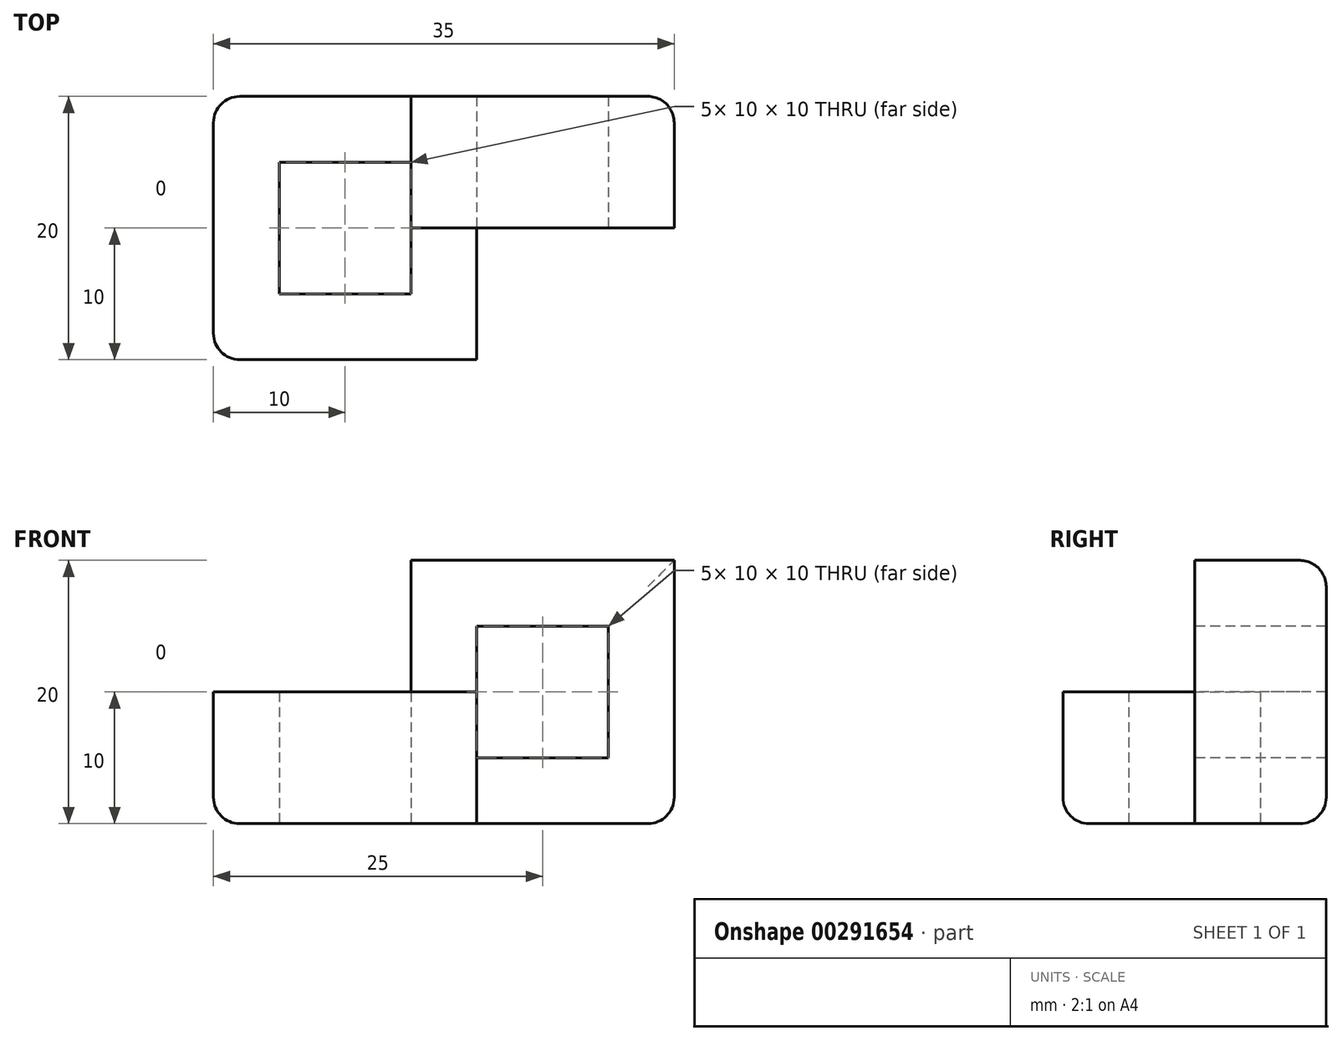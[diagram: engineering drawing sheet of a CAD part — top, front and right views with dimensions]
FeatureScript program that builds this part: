
annotation { "Feature Type Name" : "Feature", "Feature Type Description" : "" }
export const myFeature = defineFeature(function(context is Context, id is Id, definition is map)
    precondition{}
    {
        {
            var Q0;
            Q0=qCreatedBy(makeId("Top.planeOp"),FACE);
            var sketch = newSketch(context, id + "F0", { "sketchPlane" : qUnion([Q0])});
            skLineSegment(sketch, "E0.bottom", {"start": v(0, 0) * mm, "end": v(10, 0) * mm});
            skLineSegment(sketch, "E0.top", {"start": v(0, 10) * mm, "end": v(10, 10) * mm});
            skLineSegment(sketch, "E0.left", {"start": v(0, 0) * mm, "end": v(0, 10) * mm});
            skLineSegment(sketch, "E0.right", {"start": v(10, 0) * mm, "end": v(10, 10) * mm});
            skLineSegment(sketch, "E1.bottom", {"start": v(-5, 15) * mm, "end": v(30, 15) * mm});
            skLineSegment(sketch, "E1.top", {"start": v(-5, -5) * mm, "end": v(30, -5) * mm});
            skLineSegment(sketch, "E1.left", {"start": v(-5, 15) * mm, "end": v(-5, -5) * mm});
            skLineSegment(sketch, "E1.right", {"start": v(30, 15) * mm, "end": v(30, -5) * mm});
            skSolve(sketch);
        }
        {
            var Q0;
            Q0=makeQuery(id+"F0.imprint","IMPRINT",FACE,{"disambiguationData":[TD([[makeQuery(id+"F0.imprint","IMPRINT",EDGE,{"derivedFrom":sQuery(id+"F0.wireOp",EDGE,"E0.bottom")}),-1.0]])]});
            extrude(context, id + "F1", {"entities" : qUnion([Q0]), "depth" : 20 * mm});
        }
        {
            var Q0;
            Q0=makeQuery(id+"F1.opExtrude","SWEPT_FACE",FACE,{"disambiguationData":[OSD([sQuery(id+"F0.wireOp",EDGE,"E1.top")])]});
            var sketch = newSketch(context, id + "F2", { "sketchPlane" : qUnion([Q0])});
            skLineSegment(sketch, "E2.bottom", {"start": v(15, 15) * mm, "end": v(25, 15) * mm});
            skLineSegment(sketch, "E2.top", {"start": v(15, 5) * mm, "end": v(25, 5) * mm});
            skLineSegment(sketch, "E2.left", {"start": v(15, 15) * mm, "end": v(15, 5) * mm});
            skLineSegment(sketch, "E2.right", {"start": v(25, 15) * mm, "end": v(25, 5) * mm});
            skLineSegment(sketch, "E3", {"start": v(10, 20) * mm, "end": v(10, 0) * mm});
            skLineSegment(sketch, "E4", {"start": v(-5, 10) * mm, "end": v(30, 10) * mm});
            skLineSegment(sketch, "E5", {"start": v(15, 5) * mm, "end": v(15, 0) * mm});
            skSolve(sketch);
        }
        {
            var Q0;
            Q0=makeQuery(id+"F2.imprint","IMPRINT",FACE,{"disambiguationData":[TD([[makeQuery(id+"F2.imprint","IMPRINT",EDGE,{"derivedFrom":sQuery(id+"F2.wireOp",EDGE,"E2.bottom")}),-1.0]])]});
            var Q1;
            {var subQ0=sQuery(id+"F2.wireOp",EDGE,"E2.top");Q1=makeQuery(id+"F2.imprint","IMPRINT",FACE,{"disambiguationData":[TD([[makeQuery(id+"F2.imprint","IMPRINT",EDGE,{"derivedFrom":subQ0}),1.0]])]});}
            extrude(context, id + "F3", {"entities" : qUnion([Q0, Q1]), "operationType" : NewBodyOperationType.REMOVE, "oppositeDirection" : true, "depth" : 25 * mm});
        }
        {
            var Q0;
            Q0=makeQuery(id+"F1.opExtrude","CAP_FACE",FACE,{"disambiguationData":[OSD([sQuery(id+"F0.wireOp",EDGE,"E0.bottom"),sQuery(id+"F0.wireOp",EDGE,"E0.top"),sQuery(id+"F0.wireOp",EDGE,"E0.left"),sQuery(id+"F0.wireOp",EDGE,"E0.right"),sQuery(id+"F0.wireOp",EDGE,"E1.bottom"),sQuery(id+"F0.wireOp",EDGE,"E1.top"),sQuery(id+"F0.wireOp",EDGE,"E1.left"),sQuery(id+"F0.wireOp",EDGE,"E1.right")])],"isStart":false});
            var sketch = newSketch(context, id + "F4", { "sketchPlane" : qUnion([Q0])});
            skLineSegment(sketch, "E6", {"start": v(10, 15) * mm, "end": v(10, -5) * mm});
            skSolve(sketch);
        }
        {
            var Q0;
            {var subQ1=makeQuery(id+"F1.opExtrude","CAP_EDGE",EDGE,{"disambiguationData":[OSD([sQuery(id+"F0.wireOp",EDGE,"E0.bottom")])],"isStart":false});Q0=makeQuery(id+"F4.imprint","IMPRINT",FACE,{"disambiguationData":[TD([[makeQuery(id+"F4.imprint","IMPRINT",EDGE,{"derivedFrom":subQ1}),-1.0]])]});}
            extrude(context, id + "F5", {"entities" : qUnion([Q0]), "operationType" : NewBodyOperationType.REMOVE, "oppositeDirection" : true, "depth" : 10 * mm});
        }
        {
            var Q0;
            {var subQ7=sQuery(id+"F2.wireOp",EDGE,"E2.bottom");Q0=makeQuery(id+"F2.imprint","IMPRINT",FACE,{"disambiguationData":[TD([[makeQuery(id+"F2.imprint","IMPRINT",EDGE,{"derivedFrom":subQ7}),1.0]])]});}
            var Q1;
            {var subQ1=sQuery(id+"F2.wireOp",EDGE,"E2.top");Q1=makeQuery(id+"F2.imprint","IMPRINT",FACE,{"disambiguationData":[TD([[makeQuery(id+"F2.imprint","IMPRINT",EDGE,{"derivedFrom":subQ1}),-1.0]])]});}
            extrude(context, id + "F6", {"entities" : qUnion([Q0, Q1]), "operationType" : NewBodyOperationType.REMOVE, "oppositeDirection" : true, "depth" : 10 * mm});
        }
        {
            var Q0;
            Q0=makeQuery(id+"F5.boolean.opBoolean","COPY",EDGE,{"derivedFrom":makeQuery(id+"F5.opExtrude","CAP_EDGE",EDGE,{"disambiguationData":[OSD([sQuery(id+"F0.wireOp",EDGE,"E1.left")])],"isStart":false})});
            var Q1;
            Q1=makeQuery(id+"F6.boolean.opBoolean","MERGE",EDGE,{"derivedFrom":[makeQuery(id+"F5.boolean.opBoolean","COPY",EDGE,{"derivedFrom":makeQuery(id+"F5.opExtrude","CAP_EDGE",EDGE,{"disambiguationData":[OSD([sQuery(id+"F0.wireOp",EDGE,"E1.top")])],"isStart":false})}),makeQuery(id+"F6.opExtrude","CAP_EDGE",EDGE,{"disambiguationData":[OSD([sQuery(id+"F2.wireOp",EDGE,"E4")])],"isStart":true})]});
            var Q2;
            Q2=makeQuery(id+"F5.boolean.opBoolean","COPY",EDGE,{"derivedFrom":makeQuery(id+"F5.opExtrude","CAP_EDGE",EDGE,{"disambiguationData":[OSD([sQuery(id+"F0.wireOp",EDGE,"E1.bottom")])],"isStart":false})});
            var Q3;
            Q3=makeQuery(id+"F5.boolean.opBoolean","COPY",EDGE,{"derivedFrom":makeQuery(id+"F5.opExtrude","SWEPT_EDGE",EDGE,{"disambiguationData":[OSD([sQuery(id+"F0.wireOp",EDGE,"E1.bottom"),sQuery(id+"F4.wireOp",EDGE,"E6")])]})});
            var Q4;
            {var subQ0=sQuery(id+"F4.wireOp",EDGE,"E6");Q4=makeQuery(id+"F5.boolean.opBoolean","MERGE",EDGE,{"derivedFrom":[makeQuery(id+"F1.opExtrude","CAP_EDGE",EDGE,{"disambiguationData":[OSD([sQuery(id+"F0.wireOp",EDGE,"E0.right")])],"isStart":false}),makeQuery(id+"F5.opExtrude","CAP_EDGE",EDGE,{"disambiguationData":[OSD([subQ0]),TDD([makeQuery(id+"F4.imprint","IMPRINT",EDGE,{"disambiguationData":[TD([[makeQuery(id+"F4.imprint","INTERSECT",VERTEX,{"derivedFrom":[makeQuery(id+"F1.opExtrude","CAP_EDGE",EDGE,{"disambiguationData":[OSD([sQuery(id+"F0.wireOp",EDGE,"E0.top")])],"isStart":false}),subQ0]}),1.0],[makeQuery(id+"F4.imprint","INTERSECT",VERTEX,{"derivedFrom":[makeQuery(id+"F1.opExtrude","CAP_EDGE",EDGE,{"disambiguationData":[OSD([sQuery(id+"F0.wireOp",EDGE,"E1.bottom")])],"isStart":false}),subQ0]}),-1.0]])],"derivedFrom":subQ0})])],"isStart":true}),makeQuery(id+"F5.opExtrude","CAP_EDGE",EDGE,{"disambiguationData":[OSD([subQ0]),TDD([makeQuery(id+"F4.imprint","IMPRINT",EDGE,{"disambiguationData":[TD([[makeQuery(id+"F4.imprint","INTERSECT",VERTEX,{"derivedFrom":[makeQuery(id+"F1.opExtrude","CAP_EDGE",EDGE,{"disambiguationData":[OSD([sQuery(id+"F0.wireOp",EDGE,"E0.bottom")])],"isStart":false}),subQ0]}),-1.0],[makeQuery(id+"F4.imprint","INTERSECT",VERTEX,{"derivedFrom":[makeQuery(id+"F1.opExtrude","CAP_EDGE",EDGE,{"disambiguationData":[OSD([sQuery(id+"F0.wireOp",EDGE,"E1.top")])],"isStart":false}),subQ0]}),1.0]])],"derivedFrom":subQ0})])],"isStart":true})]});}
            var Q5;
            Q5=makeQuery(id+"F1.opExtrude","CAP_EDGE",EDGE,{"disambiguationData":[OSD([sQuery(id+"F0.wireOp",EDGE,"E1.bottom")])],"isStart":false});
            var Q6;
            Q6=makeQuery(id+"F1.opExtrude","SWEPT_EDGE",EDGE,{"disambiguationData":[OSD([sQuery(id+"F0.wireOp",EDGE,"E1.bottom"),sQuery(id+"F0.wireOp",EDGE,"E1.right")])]});
            var Q7;
            Q7=makeQuery(id+"F1.opExtrude","CAP_EDGE",EDGE,{"disambiguationData":[OSD([sQuery(id+"F0.wireOp",EDGE,"E1.bottom")])],"isStart":true});
            var Q8;
            Q8=makeQuery(id+"F1.opExtrude","SWEPT_EDGE",EDGE,{"disambiguationData":[OSD([sQuery(id+"F0.wireOp",EDGE,"E1.bottom"),sQuery(id+"F0.wireOp",EDGE,"E1.left")])]});
            var Q9;
            Q9=makeQuery(id+"F1.opExtrude","SWEPT_EDGE",EDGE,{"disambiguationData":[OSD([sQuery(id+"F0.wireOp",EDGE,"E1.top"),sQuery(id+"F0.wireOp",EDGE,"E1.left")])]});
            var Q10;
            Q10=makeQuery(id+"F1.opExtrude","CAP_EDGE",EDGE,{"disambiguationData":[OSD([sQuery(id+"F0.wireOp",EDGE,"E1.right")])],"isStart":true});
            var Q11;
            {var subQ0=sQuery(id+"F0.wireOp",EDGE,"E1.top");var subQ1=makeQuery(id+"F1.opExtrude","CAP_EDGE",EDGE,{"disambiguationData":[OSD([subQ0])],"isStart":true});Q11=makeQuery(id+"F6.boolean.opBoolean","COPY",EDGE,{"derivedFrom":makeQuery(id+"F6.opExtrude","CAP_EDGE",EDGE,{"disambiguationData":[OSD([subQ0]),TDD([makeQuery(id+"F2.imprint","IMPRINT",EDGE,{"disambiguationData":[TD([[makeQuery(id+"F2.imprint","INTERSECT",VERTEX,{"derivedFrom":[subQ1,sQuery(id+"F2.wireOp",EDGE,"E5")]}),-1.0]])],"derivedFrom":subQ1})])],"isStart":false})});}
            var Q12;
            Q12=makeQuery(id+"F6.boolean.opBoolean","COPY",EDGE,{"derivedFrom":makeQuery(id+"F6.opExtrude","SWEPT_EDGE",EDGE,{"disambiguationData":[OSD([sQuery(id+"F0.wireOp",EDGE,"E1.top"),sQuery(id+"F2.wireOp",EDGE,"E5")])]})});
            var Q13;
            Q13=makeQuery(id+"F6.boolean.opBoolean","COPY",EDGE,{"derivedFrom":makeQuery(id+"F6.opExtrude","CAP_EDGE",EDGE,{"disambiguationData":[OSD([sQuery(id+"F0.wireOp",EDGE,"E1.top"),sQuery(id+"F0.wireOp",EDGE,"E1.right")])],"isStart":false})});
            var Q14;
            {var subQ0=sQuery(id+"F0.wireOp",EDGE,"E1.top");var subQ1=makeQuery(id+"F1.opExtrude","CAP_EDGE",EDGE,{"disambiguationData":[OSD([subQ0])],"isStart":false});Q14=makeQuery(id+"F6.boolean.opBoolean","COPY",EDGE,{"derivedFrom":makeQuery(id+"F6.opExtrude","CAP_EDGE",EDGE,{"disambiguationData":[OSD([subQ0]),TDD([makeQuery(id+"F2.imprint","IMPRINT",EDGE,{"disambiguationData":[TD([[makeQuery(id+"F2.imprint","INTERSECT",VERTEX,{"derivedFrom":[subQ1,sQuery(id+"F2.wireOp",EDGE,"E3")]}),-1.0]])],"derivedFrom":subQ1})])],"isStart":false})});}
            var Q15;
            Q15=makeQuery(id+"F1.opExtrude","CAP_EDGE",EDGE,{"disambiguationData":[OSD([sQuery(id+"F0.wireOp",EDGE,"E1.top")])],"isStart":true});
            var Q16;
            Q16=makeQuery(id+"F1.opExtrude","CAP_EDGE",EDGE,{"disambiguationData":[OSD([sQuery(id+"F0.wireOp",EDGE,"E1.left")])],"isStart":true});
            fillet(context, id + "F7", {"entities" : qUnion([Q0, Q1, Q2, Q3, Q4, Q5, Q6, Q7, Q8, Q9, Q10, Q11, Q12, Q13, Q14, Q15, Q16]), "radius" : 2 * mm, "tangentPropagation" : true, "allowEdgeOverflow" : false});
        }
    });
